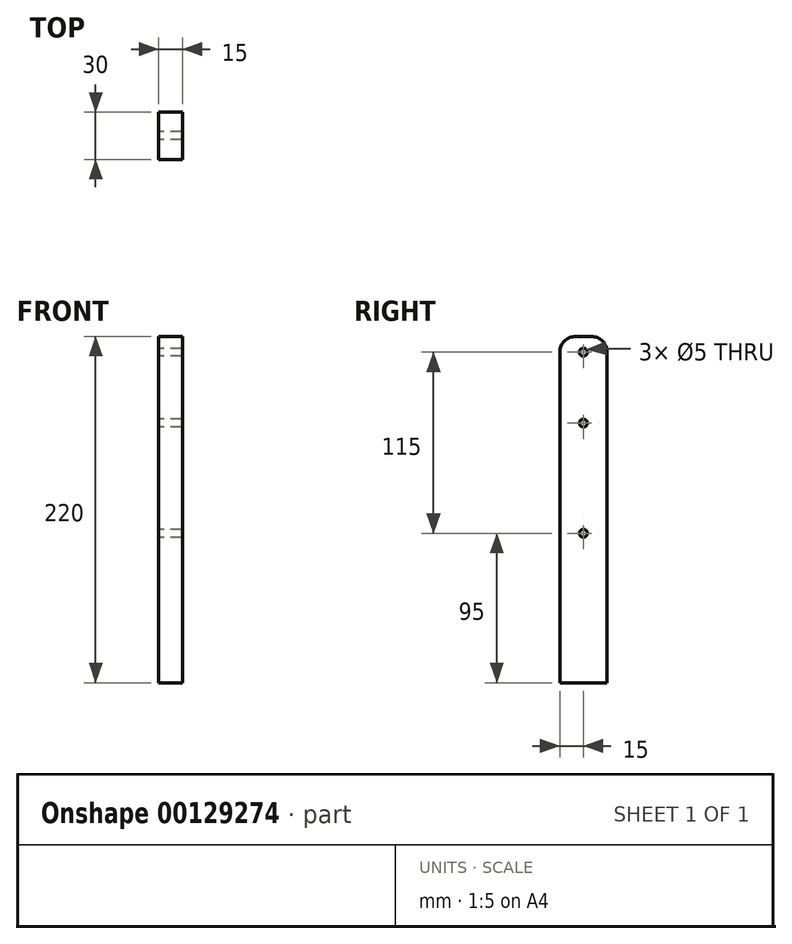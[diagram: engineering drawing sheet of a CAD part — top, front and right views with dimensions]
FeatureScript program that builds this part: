
annotation { "Feature Type Name" : "Feature", "Feature Type Description" : "" }
export const myFeature = defineFeature(function(context is Context, id is Id, definition is map)
    precondition{}
    {
        {
            var Q0;
            Q0=qCreatedBy(makeId("Right.planeOp"),FACE);
            var sketch = newSketch(context, id + "F0", { "sketchPlane" : qUnion([Q0])});
            skLineSegment(sketch, "E0.bottom", {"start": v(0, 0) * mm, "end": v(30, 0) * mm});
            skLineSegment(sketch, "E0.top", {"start": v(10, 220) * mm, "end": v(20, 220) * mm});
            skLineSegment(sketch, "E0.left", {"start": v(0, 0) * mm, "end": v(0, 210) * mm});
            skLineSegment(sketch, "E0.right", {"start": v(30, 0) * mm, "end": v(30, 210) * mm});
            skPoint(sketch, "E1.visualSharp", {"position": v(0, 220) * mm});
            skArc(sketch, "E1.filletArc", {"start": v(10, 220) * mm, "mid": v(2.93, 217.07) * mm, "end": v(0, 210) * mm});
            skPoint(sketch, "E2.visualSharp", {"position": v(30, 220) * mm});
            skArc(sketch, "E2.filletArc", {"start": v(30, 210) * mm, "mid": v(27.07, 217.07) * mm, "end": v(20, 220) * mm});
            skCircle(sketch, "E3", {"center": v(15, 210) * mm, "radius": 2.5 * mm});
            skPoint(sketch, "E3.centerSnap0", {"position": v(15, 220) * mm});
            skCircle(sketch, "E4", {"center": v(15, 165) * mm, "radius": 2.5 * mm});
            skCircle(sketch, "E5", {"center": v(15, 95) * mm, "radius": 2.5 * mm});
            skSolve(sketch);
        }
        {
            var Q0;
            Q0=makeQuery(id+"F0.imprint","IMPRINT",FACE,{"disambiguationData":[TD([[makeQuery(id+"F0.imprint","IMPRINT",EDGE,{"derivedFrom":sQuery(id+"F0.wireOp",EDGE,"E0.bottom")}),1.0]])]});
            extrude(context, id + "F1", {"entities" : qUnion([Q0]), "depth" : 15 * mm});
        }
    });
